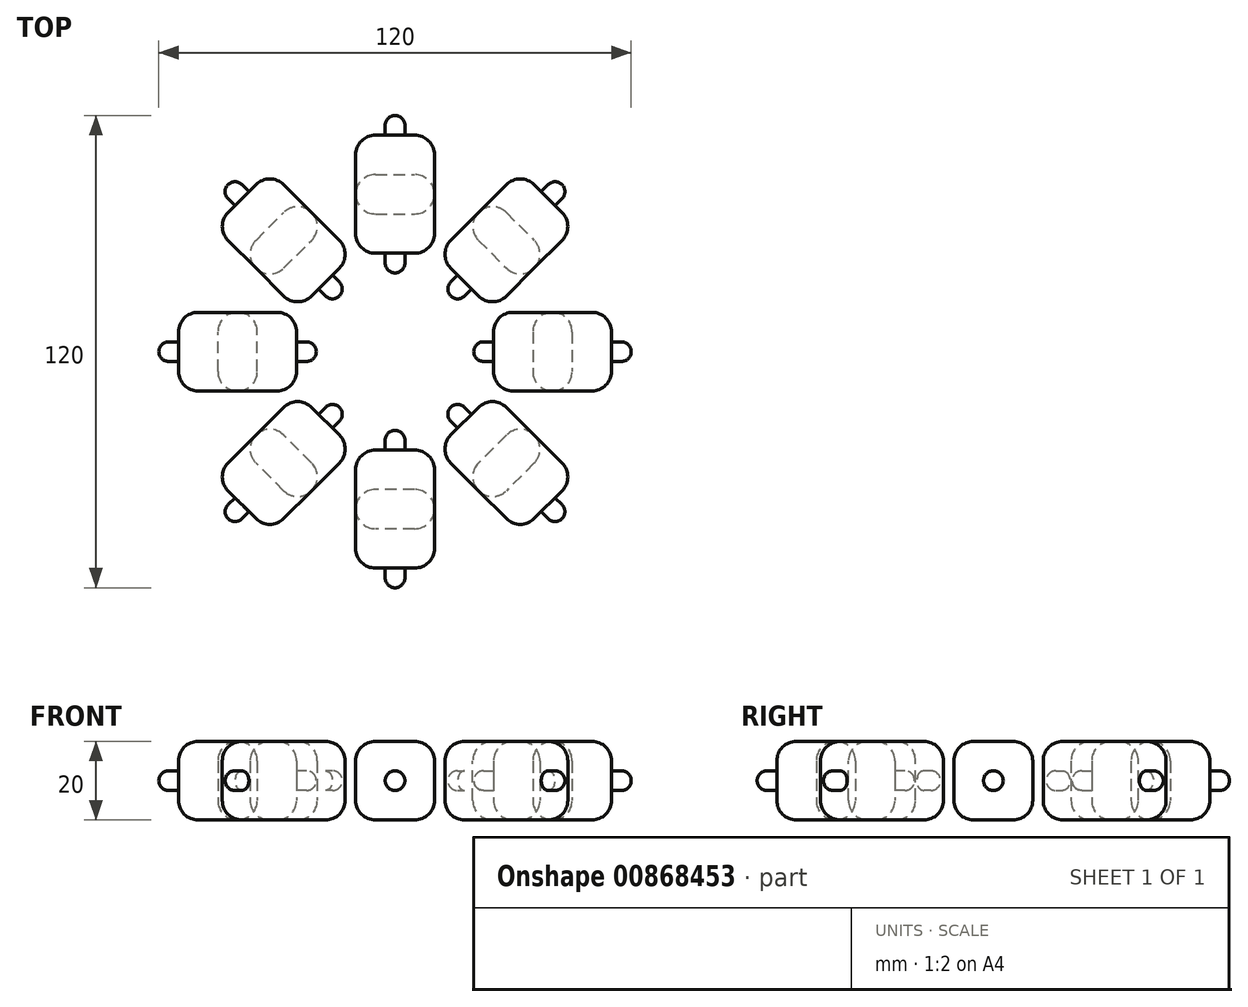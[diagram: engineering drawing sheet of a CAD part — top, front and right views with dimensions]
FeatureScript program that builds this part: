
annotation { "Feature Type Name" : "Feature", "Feature Type Description" : "" }
export const myFeature = defineFeature(function(context is Context, id is Id, definition is map)
    precondition{}
    {
        {
            var Q0;
            Q0=qCreatedBy(makeId("Top.planeOp"),FACE);
            var sketch = newSketch(context, id + "F0", { "sketchPlane" : qUnion([Q0])});
            skLineSegment(sketch, "E0.bottom", {"start": v(0, 0) * mm, "end": v(20, 0) * mm});
            skLineSegment(sketch, "E0.top", {"start": v(0, 20) * mm, "end": v(20, 20) * mm});
            skLineSegment(sketch, "E0.left", {"start": v(0, 0) * mm, "end": v(0, 20) * mm});
            skLineSegment(sketch, "E0.right", {"start": v(20, 0) * mm, "end": v(20, 20) * mm});
            skSolve(sketch);
        }
        {
            var Q0;
            Q0=makeQuery(id+"F0.imprint","IMPRINT",FACE,{"disambiguationData":[TD([[makeQuery(id+"F0.imprint","IMPRINT",EDGE,{"derivedFrom":sQuery(id+"F0.wireOp",EDGE,"E0.bottom")}),1.0]])]});
            extrude(context, id + "F1", {"entities" : qUnion([Q0]), "depth" : 20 * mm, "offsetDistance" : 25 * mm});
        }
        {
            var Q0;
            Q0=makeQuery(id+"F1.opExtrude","SWEPT_EDGE",EDGE,{"disambiguationData":[OSD([sQuery(id+"F0.wireOp",EDGE,"E0.top"),sQuery(id+"F0.wireOp",EDGE,"E0.right")])]});
            var Q1;
            Q1=makeQuery(id+"F1.opExtrude","SWEPT_EDGE",EDGE,{"disambiguationData":[OSD([sQuery(id+"F0.wireOp",EDGE,"E0.bottom"),sQuery(id+"F0.wireOp",EDGE,"E0.right")])]});
            var Q2;
            Q2=makeQuery(id+"F1.opExtrude","CAP_EDGE",EDGE,{"disambiguationData":[OSD([sQuery(id+"F0.wireOp",EDGE,"E0.right")])],"isStart":false});
            var Q3;
            Q3=makeQuery(id+"F1.opExtrude","CAP_EDGE",EDGE,{"disambiguationData":[OSD([sQuery(id+"F0.wireOp",EDGE,"E0.right")])],"isStart":true});
            var Q4;
            Q4=makeQuery(id+"F1.opExtrude","CAP_EDGE",EDGE,{"disambiguationData":[OSD([sQuery(id+"F0.wireOp",EDGE,"E0.top")])],"isStart":true});
            var Q5;
            Q5=makeQuery(id+"F1.opExtrude","CAP_EDGE",EDGE,{"disambiguationData":[OSD([sQuery(id+"F0.wireOp",EDGE,"E0.left")])],"isStart":false});
            var Q6;
            Q6=makeQuery(id+"F1.opExtrude","CAP_EDGE",EDGE,{"disambiguationData":[OSD([sQuery(id+"F0.wireOp",EDGE,"E0.bottom")])],"isStart":false});
            var Q7;
            Q7=makeQuery(id+"F1.opExtrude","CAP_EDGE",EDGE,{"disambiguationData":[OSD([sQuery(id+"F0.wireOp",EDGE,"E0.bottom")])],"isStart":true});
            var Q8;
            Q8=makeQuery(id+"F1.opExtrude","SWEPT_EDGE",EDGE,{"disambiguationData":[OSD([sQuery(id+"F0.wireOp",EDGE,"E0.top"),sQuery(id+"F0.wireOp",EDGE,"E0.left")])]});
            var Q9;
            Q9=makeQuery(id+"F1.opExtrude","SWEPT_EDGE",EDGE,{"disambiguationData":[OSD([sQuery(id+"F0.wireOp",EDGE,"E0.bottom"),sQuery(id+"F0.wireOp",EDGE,"E0.left")])]});
            var Q10;
            Q10=makeQuery(id+"F1.opExtrude","CAP_EDGE",EDGE,{"disambiguationData":[OSD([sQuery(id+"F0.wireOp",EDGE,"E0.left")])],"isStart":true});
            var Q11;
            Q11=makeQuery(id+"F1.opExtrude","CAP_EDGE",EDGE,{"disambiguationData":[OSD([sQuery(id+"F0.wireOp",EDGE,"E0.top")])],"isStart":false});
            fillet(context, id + "F2", {"entities" : qUnion([Q0, Q1, Q2, Q3, Q4, Q5, Q6, Q7, Q8, Q9, Q10, Q11]), "radius" : 5 * mm, "tangentPropagation" : true, "allowEdgeOverflow" : false});
        }
        {
            var Q0;
            Q0=makeQuery(id+"F1.opExtrude","SWEPT_FACE",FACE,{"disambiguationData":[OSD([sQuery(id+"F0.wireOp",EDGE,"E0.bottom")])]});
            var sketch = newSketch(context, id + "F3", { "sketchPlane" : qUnion([Q0])});
            skCircle(sketch, "E1", {"center": v(10, 10) * mm, "radius": 2.5 * mm});
            skPoint(sketch, "E1.centerSnap0", {"position": v(15, 10) * mm});
            skPoint(sketch, "E1.centerSnap1", {"position": v(10, 15) * mm});
            skSolve(sketch);
        }
        {
            var Q0;
            Q0=makeQuery(id+"F3.imprint","IMPRINT",FACE,{"disambiguationData":[TD([[makeQuery(id+"F3.imprint","IMPRINT",EDGE,{"derivedFrom":sQuery(id+"F3.wireOp",EDGE,"E1")}),1.0]])]});
            extrude(context, id + "F4", {"entities" : qUnion([Q0]), "operationType" : NewBodyOperationType.ADD, "depth" : 5 * mm, "offsetDistance" : 25 * mm});
        }
        {
            var Q0;
            Q0=makeQuery(id+"F4.opExtrude","CAP_EDGE",EDGE,{"disambiguationData":[OSD([sQuery(id+"F3.wireOp",EDGE,"E1")])],"isStart":false});
            fillet(context, id + "F5", {"entities" : qUnion([Q0]), "radius" : 2.5 * mm, "tangentPropagation" : true, "allowEdgeOverflow" : false});
        }
        {
            var Q0;
            Q0=qCreatedBy(makeId("Front.planeOp"),FACE);
            cPlane(context, id + "F6", {"entities" : qUnion([Q0]), "cplaneType" : CPlaneType.OFFSET, "offset" : 25 * mm, "width" : 150 * mm, "height" : 150 * mm});
        }
        {
            var Q0;
            Q0=qCreatedBy(id+"F6.planeOp",FACE);
            var sketch = newSketch(context, id + "F7", { "sketchPlane" : qUnion([Q0])});
            skLineSegment(sketch, "E2.0.0", {"start": v(5, 15) * mm, "end": v(5, 5) * mm, "construction": true});
            skLineSegment(sketch, "E2.0.1", {"start": v(5, 5) * mm, "end": v(15, 5) * mm, "construction": true});
            skLineSegment(sketch, "E2.0.2", {"start": v(15, 5) * mm, "end": v(15, 15) * mm, "construction": true});
            skLineSegment(sketch, "E2.0.3", {"start": v(15, 15) * mm, "end": v(5, 15) * mm, "construction": true});
            skPoint(sketch, "E3", {"position": v(10, 10) * mm});
            skPoint(sketch, "E3.positionSnap0", {"position": v(15, 10) * mm});
            skPoint(sketch, "E3.positionSnap1", {"position": v(10, 15) * mm});
            skLineSegment(sketch, "E4", {"start": v(10, 15) * mm, "end": v(10, 5) * mm, "construction": true});
            skSolve(sketch);
        }
        {
            var Q0;
            Q0=makeQuery(id+"F1.opExtrude","SWEPT_FACE",FACE,{"disambiguationData":[OSD([sQuery(id+"F0.wireOp",EDGE,"E0.right")])]});
            var sketch = newSketch(context, id + "F8", { "sketchPlane" : qUnion([Q0])});
            skLineSegment(sketch, "E5.bottom", {"start": v(20, 20) * mm, "end": v(0, 20) * mm});
            skLineSegment(sketch, "E5.top", {"start": v(20, 0) * mm, "end": v(0, 0) * mm});
            skLineSegment(sketch, "E5.left", {"start": v(20, 20) * mm, "end": v(20, 0) * mm});
            skLineSegment(sketch, "E5.right", {"start": v(0, 20) * mm, "end": v(0, 12.5) * mm});
            skPoint(sketch, "E5.middle", {"position": v(10, 10) * mm});
            skPoint(sketch, "E5.middle.positionSnap0", {"position": v(15, 10) * mm});
            skPoint(sketch, "E5.middle.positionSnap1", {"position": v(10, 15) * mm});
            skPoint(sketch, "E5.centerSnap0", {"position": v(15, 10) * mm});
            skPoint(sketch, "E5.centerSnap1", {"position": v(10, 15) * mm});
            skLineSegment(sketch, "E6", {"start": v(0, 10) * mm, "end": v(0, 12.5) * mm, "construction": true});
            skLineSegment(sketch, "E7", {"start": v(0, 12.5) * mm, "end": v(-2.5, 12.5) * mm});
            skLineSegment(sketch, "E8", {"start": v(-2.5, 12.5) * mm, "end": v(-2.5, 7.5) * mm, "construction": true});
            skLineSegment(sketch, "E9", {"start": v(-2.5, 7.5) * mm, "end": v(0, 7.5) * mm});
            skArc(sketch, "E10", {"start": v(-2.5, 12.5) * mm, "mid": v(-5, 10) * mm, "end": v(-2.5, 7.5) * mm});
            skLineSegment(sketch, "E11", {"start": v(0, 12.5) * mm, "end": v(0, 7.5) * mm, "construction": true});
            skLineSegment(sketch, "E12", {"start": v(0, 7.5) * mm, "end": v(0, 0) * mm});
            skSolve(sketch);
        }
        {
            var Q0;
            Q0=qCreatedBy(makeId("Front.planeOp"),FACE);
            cPlane(context, id + "F9", {"entities" : qUnion([Q0]), "cplaneType" : CPlaneType.OFFSET, "offset" : 15 * mm, "oppositeDirection" : true, "width" : 150 * mm, "height" : 150 * mm});
        }
        {
            var Q0;
            Q0=makeQuery(id+"F1.opExtrude","SWEPT_BODY",BODY,{"disambiguationData":[OSD([sQuery(id+"F0.wireOp",EDGE,"E0.bottom"),sQuery(id+"F0.wireOp",EDGE,"E0.top"),sQuery(id+"F0.wireOp",EDGE,"E0.left"),sQuery(id+"F0.wireOp",EDGE,"E0.right")])]});
            var Q1;
            Q1=qCreatedBy(id+"F9.planeOp",FACE);
            mirror(context, id + "F10", {"entities" : qUnion([Q0]), "mirrorPlane" : qUnion([Q1])});
        }
        {
            var Q0;
            Q0=makeQuery(id+"F1.opExtrude","SWEPT_BODY",BODY,{"disambiguationData":[OSD([sQuery(id+"F0.wireOp",EDGE,"E0.bottom"),sQuery(id+"F0.wireOp",EDGE,"E0.top"),sQuery(id+"F0.wireOp",EDGE,"E0.left"),sQuery(id+"F0.wireOp",EDGE,"E0.right")])]});
            var Q1;
            Q1=makeQuery(id+"F10.opPattern","COPY",BODY,{"derivedFrom":makeQuery(id+"F1.opExtrude","SWEPT_BODY",BODY,{"disambiguationData":[OSD([sQuery(id+"F0.wireOp",EDGE,"E0.bottom"),sQuery(id+"F0.wireOp",EDGE,"E0.top"),sQuery(id+"F0.wireOp",EDGE,"E0.left"),sQuery(id+"F0.wireOp",EDGE,"E0.right")])]}),"instanceName":"1"});
            var Q2;
            Q2=sQuery(id+"F7.wireOp",EDGE,"E4");
            circularPattern(context, id + "F11", {"entities" : qUnion([Q0, Q1]), "axis" : qUnion([Q2]), "angle" : 360 * degree, "instanceCount" : 8, "equalSpace" : true});
        }
    });
